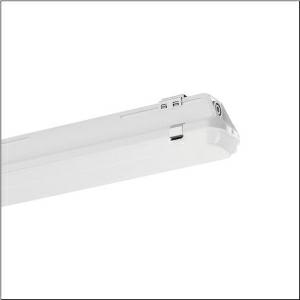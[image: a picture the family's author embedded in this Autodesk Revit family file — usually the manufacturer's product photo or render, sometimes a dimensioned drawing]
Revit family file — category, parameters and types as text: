
# Revit family: monsun_r__11_51fp208p430h_cbd4
name_source: partatom
category: Lighting Fixtures
units: mm (PartAtom-declared; Revit-internal decimal feet)

## family parameters
Cut with Voids When Loaded = No
Host = Face
Light Source = No
Part Type = Normal
Room Calculation Point = No
Round Connector Dimension = Use Diameter
Shared = No

## types (1)
- Monsun® 11 (1 x LED, 3990 lm, 24.8 W, 4000K)
    Apparent Load = 25 VA
    CIE Flux Codes = 45 75 93 94 100
    Color Rendering = 80
    Color Temperature = 4000K
    Default Elevation = 1800 mm
    Description = Monsun® 11, damp-proof luminaire, chain hanger, primary optical cover: enclosure, of PC, light emission: direct distribution, primary light characteristic: symmetric, installation type: suspended mounting, surface-mounted, horizontal mounting, vertical mounting, LED, rated luminous flux: 3.990lm, luminous efficacy: 161lm/W, light colour: 840, colour temperature: 4000K, control gear: ON/OFF, with terminal, 3-pole, max. 2.5mm², mains connection: 220..240V, AC, 50/60Hz, rated input power: 25W, luminaire housing, of glass-fibre reinforced polyester, uncoated, bright grey, incl. chain hanger, length: 1.590mm, width: 90mm, height: 88mm, clip for enclosure, of stainless steel (V2A), ceiling mounting element, of stainless steel (V2A), chain hanger, of stainless steel (V2A), protection rating (complete): IP66, insulation class (complete): insulation class I (protective earthing), certification: CE, ENEC, VDE, UKCA, protection symbol: D, impact resistance: IK08, permissible operating ambient temperature: -35..+40°C, standard: EN 50419, EN 60598-2-1, no direct snow, no direct sun, no direct rain, for indoor or canopied outdoor use, corresponds to IFS (International Featured Standards) requirements for safety and quality in the food industry, contact your sales advisor before using the luminaires in applications with unclear chemical exposure, large temperature fluctuations or condensation-forming humidity, LABS conformity tested according to VDMA 24364:2018-05, packaging unit: 1 piece
    Height = 89 mm
    Lamp = 1 x LED
    Lamp Light Flux = 3990 lm
    Lamp Power = 24.8 W
    Lamp count = 1
    Length = 1590 mm
    Luminous efficacy = 161 lm/W
    Manufacturer = Siteco
    ModVariant = No
    Model = 51FP208P430H
    Mounting Place = Ceiling
    Mounting Type = Surface mounted
    Number of Poles = 1
    OnlyDefault = Yes
    Power Factor = 1
    Product Name = Monsun® 11
    Product group = damp-proof luminaire
    ProductGroupID = 300
    Protection Class = Protection class I
    Protection Degree = IP 66
    RLX_Detail_Level = 1
    RLX_Emergency_Light_Flux = 0 lm
    RLX_Emergency_Type = 0
    RLX_Emergency_Type_DB = No
    RlxData = <blob elided: 88533 chars, md5=e253742c>
    Socket = socket
    Standby Power = 0 W
    System Light Flux = 3990 lm
    System Power = 25 W
    Type Comments = Product without accessories
    Type Image = l_1349237.jpg
    URL = http://relux.com
    VarID = ---
    Voltage = 0 V
    Weight = 0.00 kg
    Width = 90 mm

## geometry (parser evidence)
native form markers: Blend x4, Sweep x13
no freeform markers — native parametric forms only
